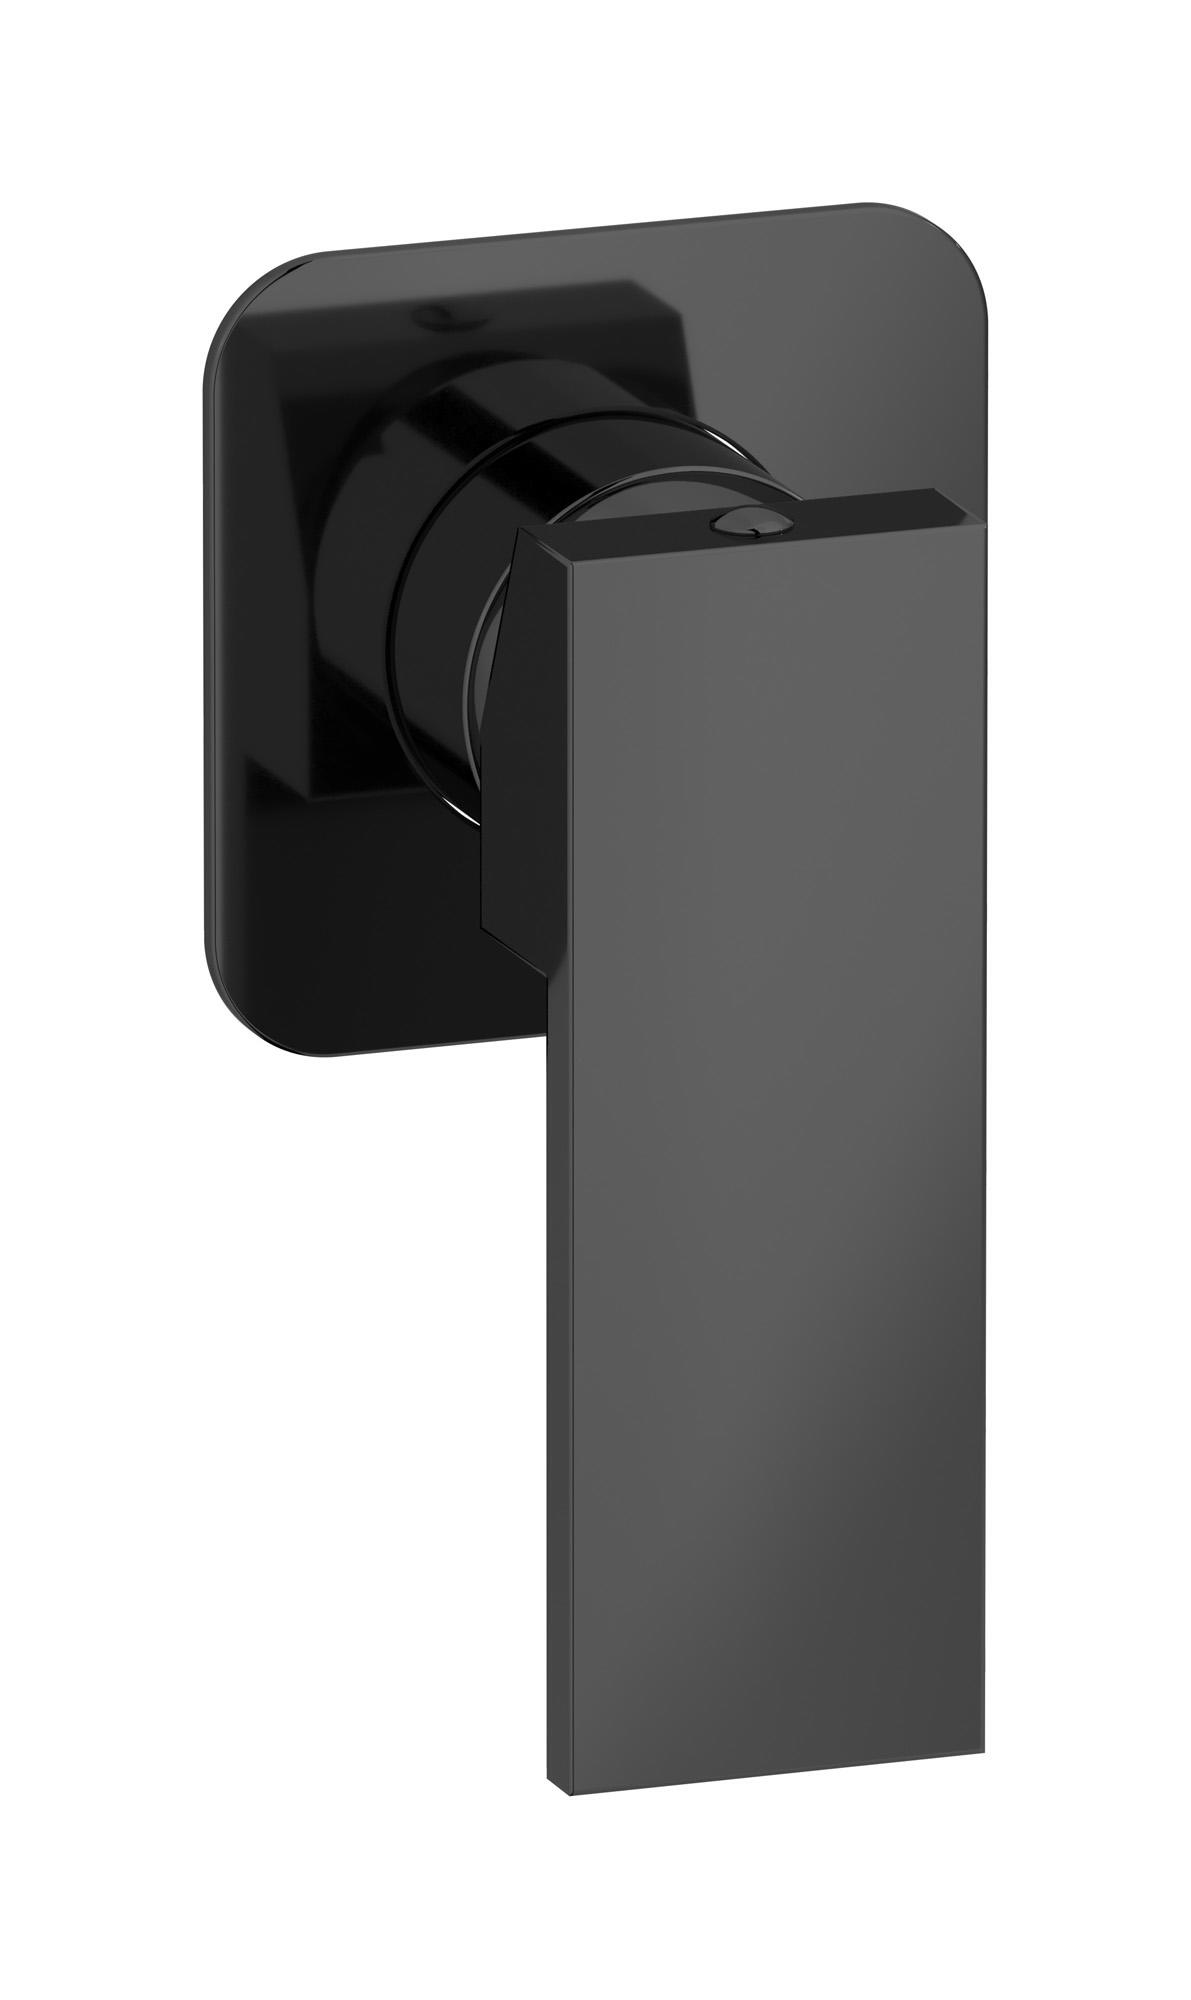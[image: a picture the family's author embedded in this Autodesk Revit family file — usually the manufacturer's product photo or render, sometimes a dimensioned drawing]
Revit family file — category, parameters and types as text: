
# Revit family: RU300
name_source: partatom
category: Apparecchi idraulici
units: mm (PartAtom-declared; Revit-internal decimal feet)

## family parameters
Basato su piano di lavoro = No
Condiviso = No
Mantieni orientamento annotazione = No
Numero OmniClass = 23.45.55.17
Punto di calcolo locali = No
Quota connettore circolare = Usa diametro
Sempre verticale = Sì
Taglio con vuoti quando caricato = No
Tipo di parte = Normale
Titolo OmniClass = Mixing Faucets

## types (12) — shared parameters
Cold water inlet = 10 mm  [stored 0.0328084 ft]
Commenti sul tipo = Exposed parts for manual wall mixer
Connessione CW = No
Connessione HW = No
Connessione di scarico = No
Connessione di ventilazione = No
Descrizione = Exposed parts for manual wall mixer
Hot water inlet = 10 mm  [stored 0.0328084 ft]
Produttore = IB Rubinetterie S.p.A.
URL = https://www.weareib.it
zero-valued in all types: Prospetto di default

## per-type parameters (varying)
| type | Finishes surface | Immagine tipo | Modello |
| Matt White | IB_matt white | RU300BO.jpg | RU300BO |
| Chrome | IB_Chrome | RU300CC.jpg | RU300CC |
| Black Chrome | IB_Black chrome | RU300CF.jpg | RU300CF |
| Brushed Black Chrome | IB_Brushed black chrome | RU300CS.jpg | RU300CS |
| Pale Gold | IB_Pale gold | RU300II.jpg | RU300II |
| Brushed Pale Gold | IB_brushed pale gold | RU300IS.jpg | RU300IS |
| Matt Black | IB_matt black | RU300NP.jpg | RU300NP |
| Gold | IB_gold | RU300OO.jpg | RU300OO |
| Brushed Gold | IB_brushed gold | RU300OS.jpg | RU300OS |
| Rose Gold | IB_Rose gold | RU300RS.jpg | RU300RS |
| Brushed Rose Gold | IB_Brushed rose gold | RU300SR.jpg | RU300SR |
| Brushed Nickel | IB_Brushed nickel | RU300SS.jpg | RU300SS |

note: [stored X ft] marks values corroborated as IEEE doubles in the binary element streams (Revit-internal decimal feet)
